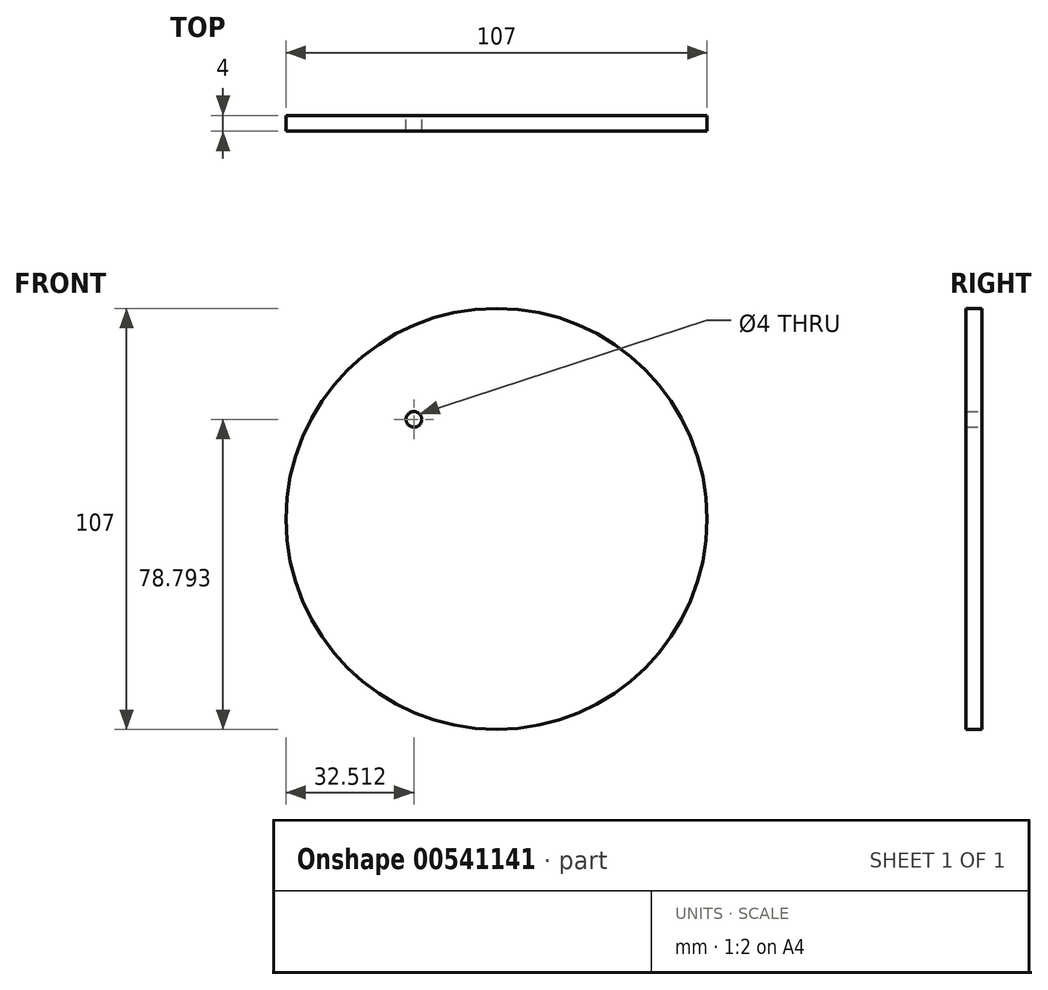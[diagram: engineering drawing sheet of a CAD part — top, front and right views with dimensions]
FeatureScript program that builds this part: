
annotation { "Feature Type Name" : "Feature", "Feature Type Description" : "" }
export const myFeature = defineFeature(function(context is Context, id is Id, definition is map)
    precondition{}
    {
        {
            var Q0;
            Q0=qCreatedBy(makeId("Front.planeOp"),FACE);
            var sketch = newSketch(context, id + "F0", { "sketchPlane" : qUnion([Q0])});
            skCircle(sketch, "E0", {"center": v(0, 0) * mm, "radius": 53.5 * mm});
            skCircle(sketch, "E1", {"center": v(-20.99, 25.3) * mm, "radius": 2 * mm});
            skSolve(sketch);
        }
        {
            var Q0;
            Q0=makeQuery(id+"F0.imprint","IMPRINT",FACE,{"disambiguationData":[TD([[makeQuery(id+"F0.imprint","IMPRINT",EDGE,{"derivedFrom":sQuery(id+"F0.wireOp",EDGE,"E0")}),1.0]])]});
            extrude(context, id + "F1", {"entities" : qUnion([Q0]), "depth" : 4 * mm, "offsetDistance" : 25 * mm});
        }
    });
